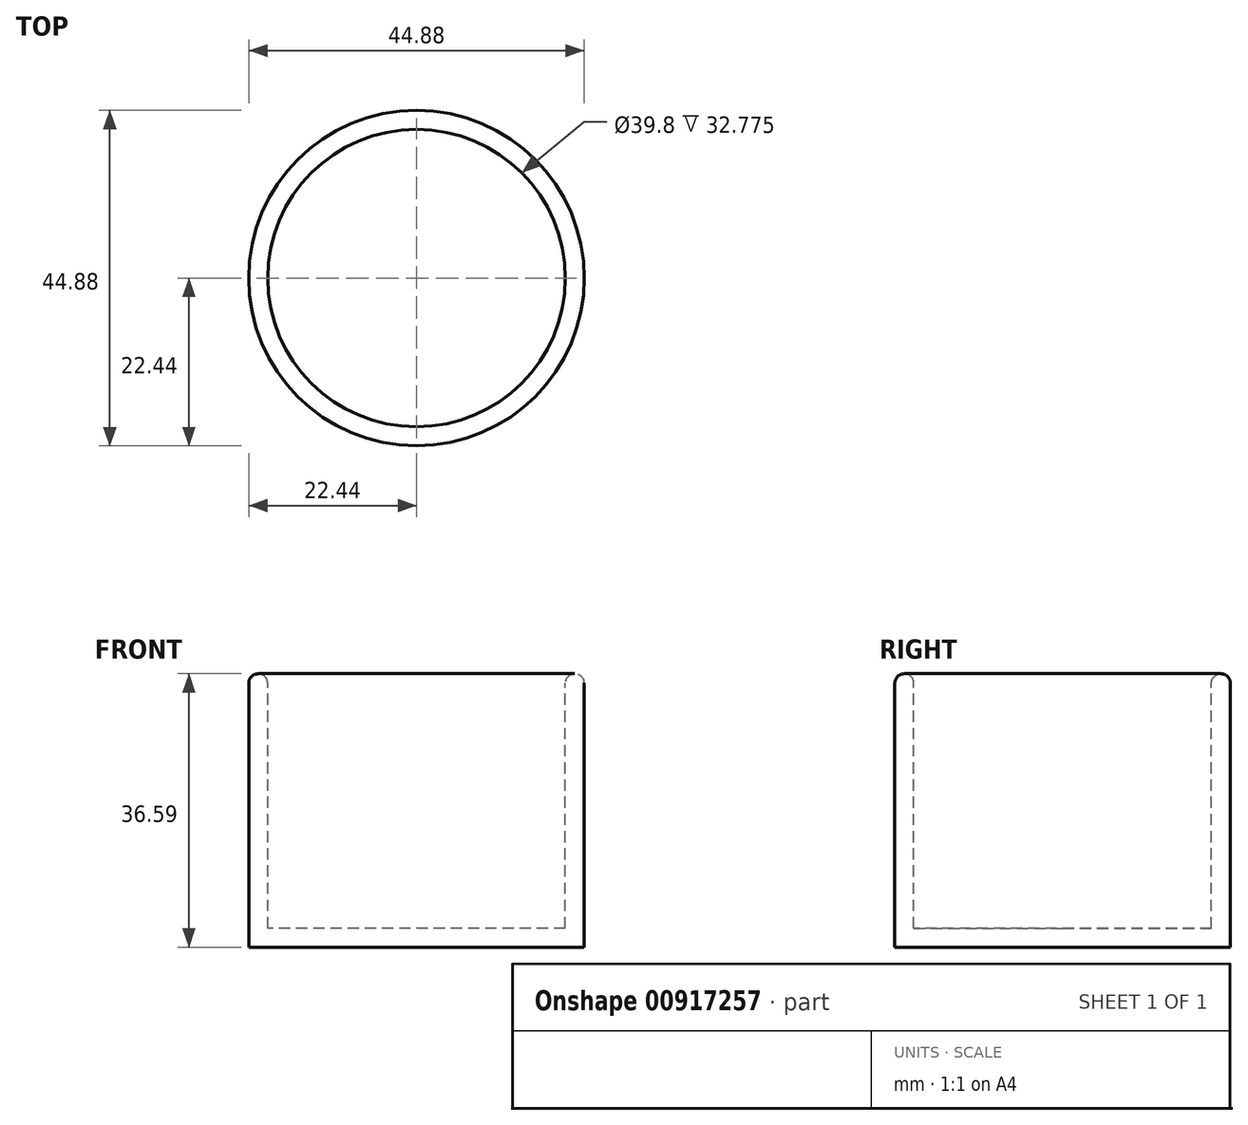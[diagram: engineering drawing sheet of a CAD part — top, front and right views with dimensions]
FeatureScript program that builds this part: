
annotation { "Feature Type Name" : "Feature", "Feature Type Description" : "" }
export const myFeature = defineFeature(function(context is Context, id is Id, definition is map)
    precondition{}
    {
        {
            var Q0;
            Q0=qCreatedBy(makeId("Front.planeOp"),FACE);
            var sketch = newSketch(context, id + "F0", { "sketchPlane" : qUnion([Q0])});
            skLineSegment(sketch, "E0", {"start": v(-22.91, 36.59) * mm, "end": v(-22.91, 0) * mm});
            skSolve(sketch);
        }
        {
            var Q0;
            Q0=qCreatedBy(makeId("Top.planeOp"),FACE);
            var sketch = newSketch(context, id + "F1", { "sketchPlane" : qUnion([Q0])});
            skCircle(sketch, "E1", {"center": v(0, 0) * mm, "radius": 22.44 * mm});
            skSolve(sketch);
        }
        {
            var Q0;
            Q0=makeQuery(id+"F1.imprint","IMPRINT",FACE,{"disambiguationData":[TD([[makeQuery(id+"F1.imprint","IMPRINT",EDGE,{"derivedFrom":sQuery(id+"F1.wireOp",EDGE,"E1")}),1.0]])]});
            var Q1;
            Q1=sQuery(id+"F0.wireOp",EDGE,"E0");
            sweep(context, id + "F2", {"profiles" : qUnion([Q0]), "path" : qUnion([Q1])});
        }
        {
            var Q0;
            Q0=makeQuery(id+"F2.opSweep","CAP_FACE",FACE,{"disambiguationData":[OSD([sQuery(id+"F0.wireOp",VERTEX,"E0.start"),sQuery(id+"F1.wireOp",EDGE,"E1")])],"isStart":false});
            shell(context, id + "F3", {"entities" : qUnion([Q0]), "thickness" : 2.54 * mm});
        }
        {
            var Q0;
            Q0=makeQuery(id+"F3.opShell","OFFSET_EDGE",EDGE,{"disambiguationData":[OSD([sQuery(id+"F0.wireOp",VERTEX,"E0.start"),sQuery(id+"F1.wireOp",EDGE,"E1")])]});
            var Q1;
            Q1=makeQuery(id+"F2.opSweep","CAP_EDGE",EDGE,{"disambiguationData":[OSD([sQuery(id+"F0.wireOp",VERTEX,"E0.start"),sQuery(id+"F1.wireOp",EDGE,"E1")])],"isStart":false});
            fillet(context, id + "F4", {"entities" : qUnion([Q0, Q1]), "radius" : 1.27 * mm, "tangentPropagation" : true, "allowEdgeOverflow" : false});
        }
    });
